# Revit family: QUEST_335_Duct
name_source: partatom
category: Mechanical Equipment
units: mm (PartAtom-declared; Revit-internal decimal feet)

## family parameters
Always vertical = Yes
Cut with Voids When Loaded = No
OmniClass Number = 23.75.00.00
OmniClass Title = Climate Control (HVAC)
Part Type = Normal
Room Calculation Point = No
Round Connector Dimension = Use Diameter
Shared = No
Work Plane-Based = No

## types (1)
- QUEST_335_Duct
    Air Filter (MERV-13) = Size 20" x 22" x 2"
    Clearance = Yes
    Current Draw (Amps) = 7.9A @ 208v    6.9 @ 230v
    Efficiency (Pints/KWh) = 9.3
    Energy Factor (L/kWh) = 4.3
    Impeller = Backward curved
    Maximun Overcurrent Protection (MOP) = 25A @ 208v   20A @ 230v
    Minimun Circuit Ampacity (MCA) = 15.8A @ 208v   14.4A @ 230v
    Operating Temperature = 56°F Min - 95°F Max
(Inlet Air Temperature)
    Power (Watts) = 1565
    Rated Current Draw (Amps) (104°F 36%) = 10.3A @ 208v   8.8A @ 230v
    Supply voltage = 208-230 VAC - 1     Phase - 60 Hz.
    Trap = Yes
    URL = https://www.questclimate.com
    Unit = Quest 335    4042500
    Water Removal ((Pints/Day) = 335

## geometry (parser evidence)
native form markers: Sweep x9
no freeform markers — native parametric forms only
